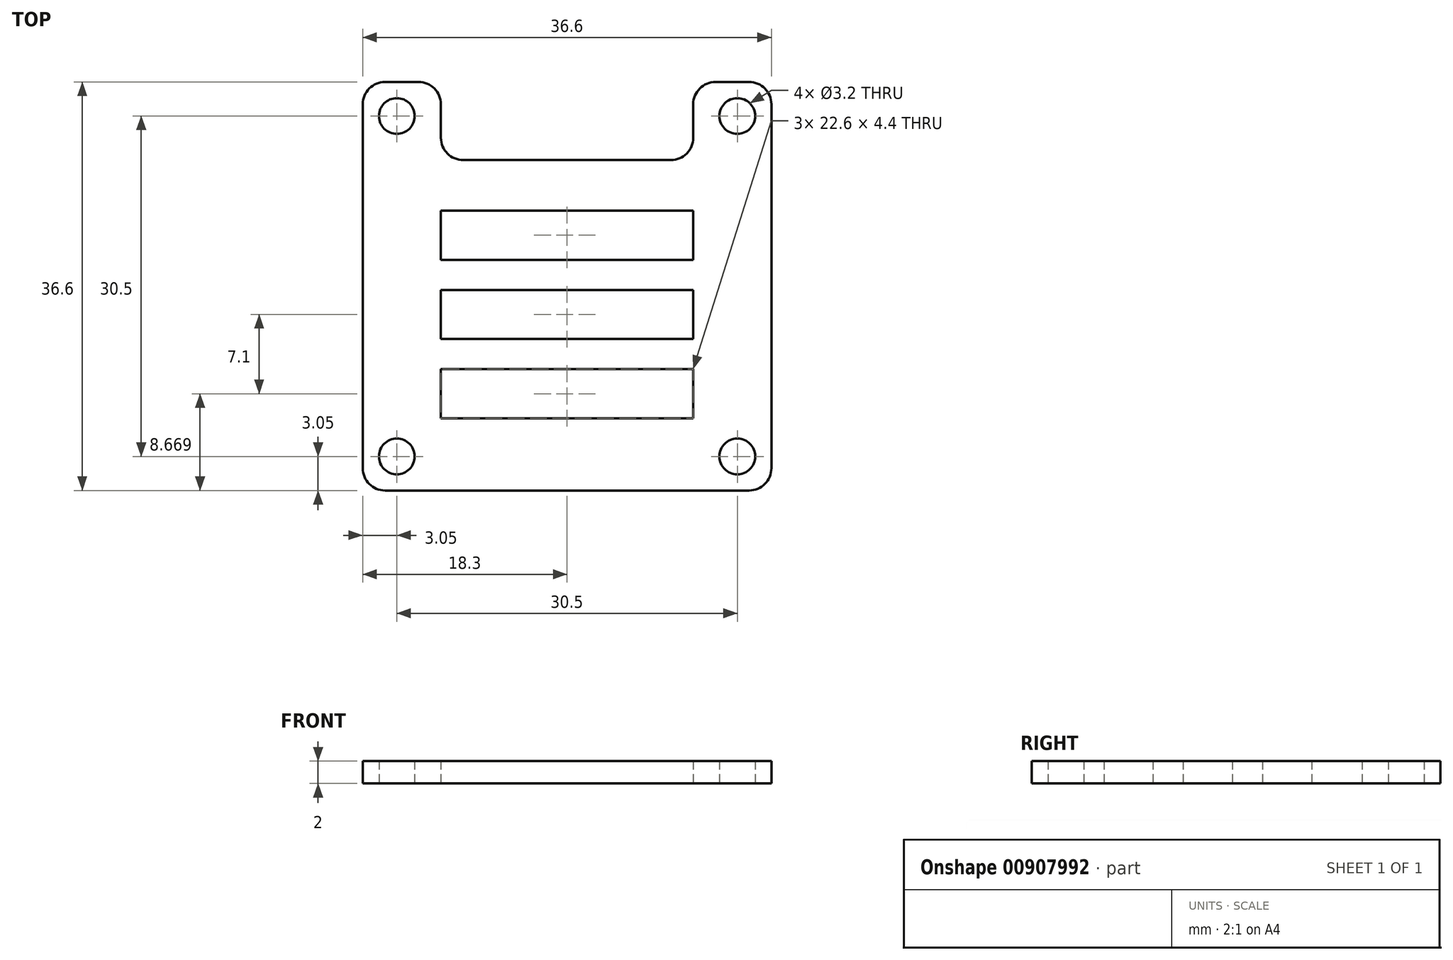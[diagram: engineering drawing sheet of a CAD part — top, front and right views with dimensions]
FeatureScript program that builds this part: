
annotation { "Feature Type Name" : "Feature", "Feature Type Description" : "" }
export const myFeature = defineFeature(function(context is Context, id is Id, definition is map)
    precondition{}
    {
        {
            var Q0;
            Q0=qCreatedBy(makeId("Top.planeOp"),FACE);
            var sketch = newSketch(context, id + "F0", { "sketchPlane" : qUnion([Q0])});
            skCircle(sketch, "E0", {"center": v(-15.25, 15.25) * mm, "radius": 1.6 * mm});
            skCircle(sketch, "E1.0.1.0", {"center": v(-15.25, -15.25) * mm, "radius": 1.6 * mm});
            skCircle(sketch, "E1.1.0.0", {"center": v(15.25, 15.25) * mm, "radius": 1.6 * mm});
            skCircle(sketch, "E1.1.1.0", {"center": v(15.25, -15.25) * mm, "radius": 1.6 * mm});
            skLineSegment(sketch, "E1.direction1", {"start": v(-15.25, 15.25) * mm, "end": v(15.25, 15.25) * mm, "construction": true});
            skLineSegment(sketch, "E1.direction2", {"start": v(-15.25, 15.25) * mm, "end": v(-15.25, -15.25) * mm, "construction": true});
            skLineSegment(sketch, "E2.bottom", {"start": v(-16.3, 18.3) * mm, "end": v(-13.3, 18.3) * mm});
            skLineSegment(sketch, "E2.top", {"start": v(-16.3, -18.3) * mm, "end": v(16.3, -18.3) * mm});
            skLineSegment(sketch, "E2.left", {"start": v(-18.3, 16.3) * mm, "end": v(-18.3, -16.3) * mm});
            skLineSegment(sketch, "E2.right", {"start": v(18.3, 16.3) * mm, "end": v(18.3, -16.3) * mm});
            skPoint(sketch, "E3.visualSharp", {"position": v(-18.3, 18.3) * mm});
            skArc(sketch, "E3.filletArc", {"start": v(-16.3, 18.3) * mm, "mid": v(-17.71, 17.71) * mm, "end": v(-18.3, 16.3) * mm});
            skPoint(sketch, "E4.visualSharp", {"position": v(18.3, 18.3) * mm});
            skArc(sketch, "E4.filletArc", {"start": v(18.3, 16.3) * mm, "mid": v(17.71, 17.71) * mm, "end": v(16.3, 18.3) * mm});
            skPoint(sketch, "E5.visualSharp", {"position": v(18.3, -18.3) * mm});
            skArc(sketch, "E5.filletArc", {"start": v(16.3, -18.3) * mm, "mid": v(17.71, -17.71) * mm, "end": v(18.3, -16.3) * mm});
            skPoint(sketch, "E6.visualSharp", {"position": v(-18.3, -18.3) * mm});
            skArc(sketch, "E6.filletArc", {"start": v(-18.3, -16.3) * mm, "mid": v(-17.71, -17.71) * mm, "end": v(-16.3, -18.3) * mm});
            skLineSegment(sketch, "E7.top", {"start": v(-9.3, 11.3) * mm, "end": v(9.3, 11.3) * mm});
            skLineSegment(sketch, "E7.left", {"start": v(-11.3, 16.3) * mm, "end": v(-11.3, 13.3) * mm});
            skLineSegment(sketch, "E7.right", {"start": v(11.3, 16.3) * mm, "end": v(11.3, 13.3) * mm});
            skLineSegment(sketch, "E8.trimOffspring", {"start": v(13.3, 18.3) * mm, "end": v(16.3, 18.3) * mm});
            skPoint(sketch, "E9.visualSharp", {"position": v(-11.3, 18.3) * mm});
            skArc(sketch, "E9.filletArc", {"start": v(-11.3, 16.3) * mm, "mid": v(-11.89, 17.71) * mm, "end": v(-13.3, 18.3) * mm});
            skPoint(sketch, "E10.visualSharp", {"position": v(11.3, 18.3) * mm});
            skArc(sketch, "E10.filletArc", {"start": v(13.3, 18.3) * mm, "mid": v(11.89, 17.71) * mm, "end": v(11.3, 16.3) * mm});
            skPoint(sketch, "E11.visualSharp", {"position": v(11.3, 11.3) * mm});
            skArc(sketch, "E11.filletArc", {"start": v(9.3, 11.3) * mm, "mid": v(10.71, 11.89) * mm, "end": v(11.3, 13.3) * mm});
            skPoint(sketch, "E12.visualSharp", {"position": v(-11.3, 11.3) * mm});
            skArc(sketch, "E12.filletArc", {"start": v(-11.3, 13.3) * mm, "mid": v(-10.71, 11.89) * mm, "end": v(-9.3, 11.3) * mm});
            skLineSegment(sketch, "E13.bottom", {"start": v(-11.3, 6.77) * mm, "end": v(11.3, 6.77) * mm});
            skLineSegment(sketch, "E13.top", {"start": v(-11.3, 2.37) * mm, "end": v(11.3, 2.37) * mm});
            skLineSegment(sketch, "E13.left", {"start": v(-11.3, 6.77) * mm, "end": v(-11.3, 2.37) * mm});
            skLineSegment(sketch, "E13.right", {"start": v(11.3, 6.77) * mm, "end": v(11.3, 2.37) * mm});
            skLineSegment(sketch, "E14.0.1.0", {"start": v(-11.3, -0.33) * mm, "end": v(11.3, -0.33) * mm});
            skLineSegment(sketch, "E14.0.1.1", {"start": v(11.3, -0.33) * mm, "end": v(11.3, -4.73) * mm});
            skLineSegment(sketch, "E14.0.1.2", {"start": v(-11.3, -0.33) * mm, "end": v(-11.3, -4.73) * mm});
            skLineSegment(sketch, "E14.0.1.3", {"start": v(-11.3, -4.73) * mm, "end": v(11.3, -4.73) * mm});
            skLineSegment(sketch, "E14.0.2.0", {"start": v(-11.3, -7.43) * mm, "end": v(11.3, -7.43) * mm});
            skLineSegment(sketch, "E14.0.2.1", {"start": v(11.3, -7.43) * mm, "end": v(11.3, -11.83) * mm});
            skLineSegment(sketch, "E14.0.2.2", {"start": v(-11.3, -7.43) * mm, "end": v(-11.3, -11.83) * mm});
            skLineSegment(sketch, "E14.0.2.3", {"start": v(-11.3, -11.83) * mm, "end": v(11.3, -11.83) * mm});
            skLineSegment(sketch, "E14.direction1", {"start": v(-11.3, 2.37) * mm, "end": v(13.7, 2.37) * mm, "construction": true});
            skLineSegment(sketch, "E14.direction2", {"start": v(-11.3, 2.37) * mm, "end": v(-11.3, -4.73) * mm, "construction": true});
            skSolve(sketch);
        }
        {
            var Q0;
            Q0=makeQuery(id+"F0.imprint","IMPRINT",FACE,{"disambiguationData":[TD([[makeQuery(id+"F0.imprint","IMPRINT",EDGE,{"derivedFrom":sQuery(id+"F0.wireOp",EDGE,"E0")}),-1.0]])]});
            extrude(context, id + "F1", {"entities" : qUnion([Q0]), "depth" : 2 * mm, "offsetDistance" : 25 * mm});
        }
    });
